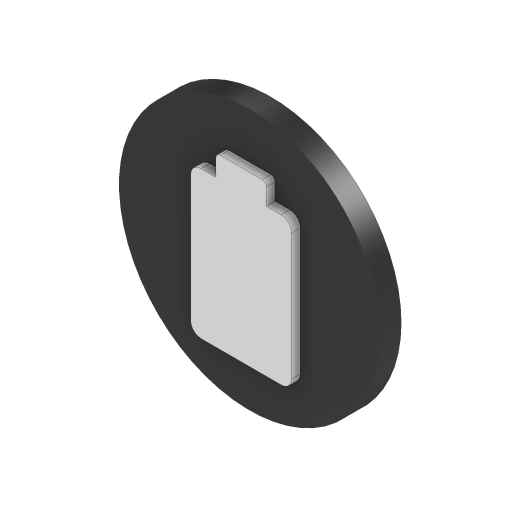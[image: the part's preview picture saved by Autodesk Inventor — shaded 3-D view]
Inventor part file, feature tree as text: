
AUTODESK INVENTOR PART (.ipt)
format: ipt  version: 2023 (Build 270158000, 158)  size: 257,024 bytes
history: native  units: mm
features: extrude x2, sketch x2, other x1
ambient origin geometry x8: Origin, YZ Plane, XZ Plane, XY Plane, X Axis, Y Axis, Z Axis, Center Point
bodies: Body1 (feature_tree)
feature tree (5):
  other  "Těleso1"
  extrude  "Vysunutí1"  Depth=12.4mm
  extrude  "Vysunutí2"  Depth=1.0mm TaperAngle=0.0deg
  sketch  "Náčrt1"
  sketch  "Náčrt2"
